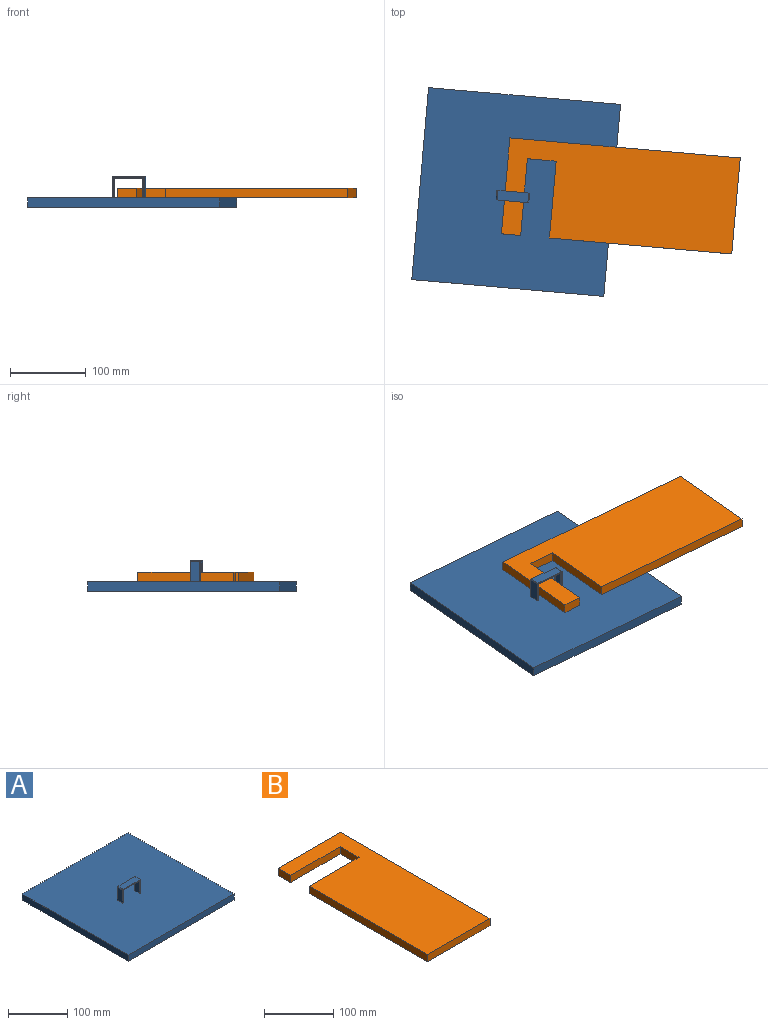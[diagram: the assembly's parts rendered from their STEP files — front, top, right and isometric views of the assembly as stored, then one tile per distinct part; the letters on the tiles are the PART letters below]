
ASSEMBLY  parts=2 mates=2
PART A: 22 faces, bbox 254x254x40.6 mm
  f0: plane 254x254mm, normal (0,0,1), area 64452.9mm2, adj f1,f2,f3,f4,f6,f7,f8,f9
  f1: plane 254x12.7mm, normal (0,-1,0), area 3225.8mm2, adj f0,f2,f4,f5
  f2: plane 254x12.7mm, normal (1,0,0), area 3225.8mm2, adj f0,f1,f3,f5
  f3: plane 254x12.7mm, normal (0,1,0), area 3225.8mm2, adj f0,f2,f4,f5
  f4: plane 254x12.7mm, normal (-1,0,0), area 3225.8mm2, adj f0,f1,f3,f5
  f5: plane 254x254mm, normal (0,0,-1), area 64516mm2, adj f1,f2,f3,f4
  f6: plane 43.18x27.94mm, normal (0,1,0), area 121.9mm2, adj f0,f7,f10,f12,f17,f18,f19,f20
  f7: plane 26.67x12.7mm, normal (-1,0,0), area 338.7mm2, adj f0,f6,f8,f21
  f8: plane 43.18x27.94mm, normal (0,-1,0), area 121.9mm2, adj f0,f7,f10,f12,f14,f15,f16,f20
  f9: plane 25.4x10.16mm, normal (1,0,0), area 258.1mm2, adj f0,f13,f15,f18
  f10: plane 40.64x12.7mm, normal (0,0,1), area 516.1mm2, adj f6,f8,f20,f21
  f11: plane 25.4x10.16mm, normal (-1,0,0), area 258.1mm2, adj f0,f13,f14,f17
  f12: plane 26.67x12.7mm, normal (1,0,0), area 338.7mm2, adj f0,f6,f8,f20
  f13: plane 38.1x10.16mm, normal (0,0,-1), area 387.1mm2, adj f9,f11,f16,f19
  f14: cylinder r=1.27mm len=26.67mm, axis (0,0,-1), area 51.6mm2, adj f0,f8,f11,f16
  f15: cylinder r=1.27mm len=26.67mm, axis (0,0,1), area 51.6mm2, adj f0,f8,f9,f16
  f16: cylinder r=1.27mm len=40.64mm, axis (-1,0,0), area 77.8mm2, adj f8,f13,f14,f15
  f17: cylinder r=1.27mm len=26.67mm, axis (0,0,1), area 51.6mm2, adj f0,f6,f11,f19
  f18: cylinder r=1.27mm len=26.67mm, axis (0,0,-1), area 51.6mm2, adj f0,f6,f9,f19
  f19: cylinder r=1.27mm len=40.64mm, axis (1,0,0), area 77.8mm2, adj f6,f13,f17,f18
  f20: cylinder r=1.27mm len=12.7mm, axis (0,-1,0), area 25.3mm2, adj f6,f8,f10,f12
  f21: cylinder r=1.27mm len=12.7mm, axis (0,1,0), area 25.3mm2, adj f6,f7,f8,f10
PART B: 10 faces, bbox 127x304.8x12.7 mm
  f0: plane 25.4x12.7mm, normal (-1,0,0), area 322.6mm2, adj f1,f2,f5,f7
  f1: plane 304.8x127mm, normal (0,0,1), area 34838.6mm2, adj f0,f3,f4,f5,f6,f7,f8,f9
  f2: plane 304.8x127mm, normal (0,0,-1), area 34838.6mm2, adj f0,f3,f4,f5,f6,f7,f8,f9
  f3: plane 127x12.7mm, normal (0,-1,0), area 1612.9mm2, adj f1,f2,f4,f6
  f4: plane 304.8x12.7mm, normal (1,0,0), area 3871mm2, adj f1,f2,f3,f5
  f5: plane 127x12.7mm, normal (0,1,0), area 1612.9mm2, adj f0,f1,f2,f4
  f6: plane 241.3x12.7mm, normal (-1,0,0), area 3064.5mm2, adj f1,f2,f3,f8
  f7: plane 101.6x12.7mm, normal (0,-1,0), area 1290.3mm2, adj f0,f1,f2,f9
  f8: plane 101.6x12.7mm, normal (0,1,0), area 1290.3mm2, adj f1,f2,f6,f9
  f9: plane 38.1x12.7mm, normal (-1,0,0), area 483.9mm2, adj f1,f2,f7,f8
PLACE A rot(axis=(0,0,-1),5deg) t=(261.11,134.76,-117.29)mm
PLACE B rot(axis=(0,0,1),85deg) t=(440.97,317.15,-104.59)mm
MATE planar B.f2 <-> A.f0  axis (0,0,-1) through (295.69,267.53,-104.59)mm
MATE parallel A.f0 <-> B.f2  axis (0,0,1) through (145.66,272.35,-104.59)mm
